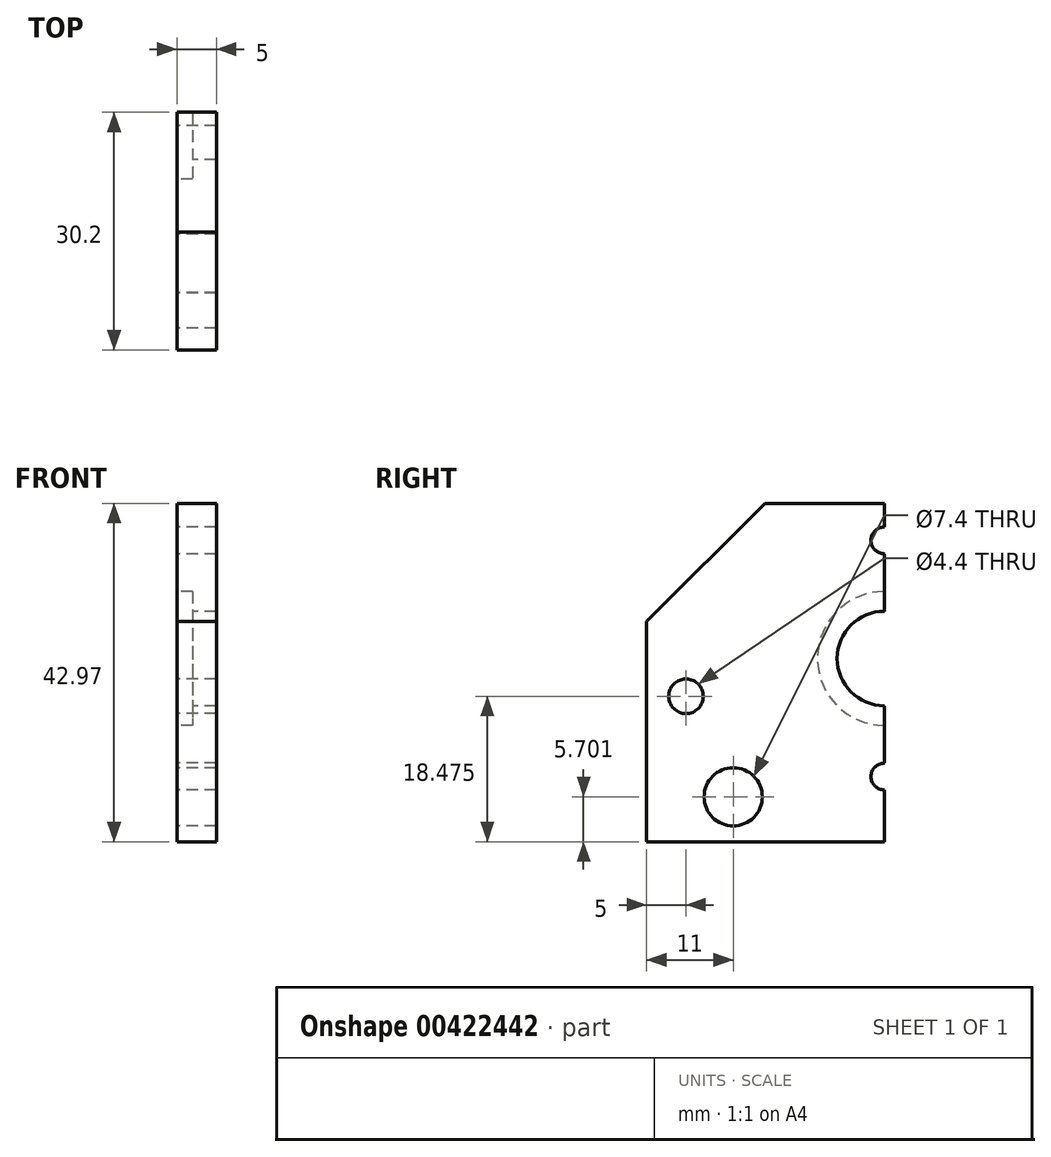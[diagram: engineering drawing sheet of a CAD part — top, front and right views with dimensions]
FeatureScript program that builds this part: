
annotation { "Feature Type Name" : "Feature", "Feature Type Description" : "" }
export const myFeature = defineFeature(function(context is Context, id is Id, definition is map)
    precondition{}
    {
        {
            var Q0;
            Q0=qCreatedBy(makeId("Right.planeOp"),FACE);
            var sketch = newSketch(context, id + "F0", { "sketchPlane" : qUnion([Q0])});
            skLineSegment(sketch, "E0.top", {"start": v(-63.57, 5.37) * mm, "end": v(-33.37, 5.37) * mm});
            skLineSegment(sketch, "E0.left", {"start": v(-63.57, 33.34) * mm, "end": v(-63.57, 5.37) * mm});
            skLineSegment(sketch, "E1", {"start": v(-48.57, 48.34) * mm, "end": v(-63.57, 33.34) * mm});
            skLineSegment(sketch, "E2", {"start": v(-48.57, 48.34) * mm, "end": v(-33.37, 48.34) * mm});
            skArc(sketch, "E3", {"start": v(-33.37, 37.14) * mm, "mid": v(-41.87, 28.64) * mm, "end": v(-33.37, 20.14) * mm});
            skPoint(sketch, "E3.first.point", {"position": v(-41.87, 28.44) * mm});
            skPoint(sketch, "E3.third.point", {"position": v(-33.88, 20.16) * mm});
            skArc(sketch, "E4", {"start": v(-33.37, 34.64) * mm, "mid": v(-39.37, 28.64) * mm, "end": v(-33.37, 22.64) * mm});
            skArc(sketch, "E5", {"start": v(-33.37, 45.34) * mm, "mid": v(-35.07, 43.64) * mm, "end": v(-33.37, 41.94) * mm});
            skPoint(sketch, "E5.first.point", {"position": v(-34.85, 44.47) * mm});
            skPoint(sketch, "E5.third.point", {"position": v(-34.4, 42.3) * mm});
            skCircle(sketch, "E6", {"center": v(-58.57, 23.84) * mm, "radius": 2.2 * mm});
            skPoint(sketch, "E6.first.point", {"position": v(-57.03, 25.41) * mm});
            skPoint(sketch, "E6.second.point", {"position": v(-60.74, 23.5) * mm});
            skPoint(sketch, "E6.third.point", {"position": v(-57.62, 21.86) * mm});
            skCircle(sketch, "E7", {"center": v(-52.57, 11.07) * mm, "radius": 3.7 * mm});
            skPoint(sketch, "E7.first.point", {"position": v(-50.08, 13.8) * mm});
            skPoint(sketch, "E7.second.point", {"position": v(-50.64, 7.91) * mm});
            skPoint(sketch, "E7.third.point", {"position": v(-56.25, 10.68) * mm});
            skArc(sketch, "E8", {"start": v(-33.37, 15.34) * mm, "mid": v(-35.07, 13.64) * mm, "end": v(-33.37, 11.94) * mm});
            skPoint(sketch, "E8.first.point", {"position": v(-33.72, 15.3) * mm});
            skPoint(sketch, "E8.second.point", {"position": v(-34.93, 12.96) * mm});
            skLineSegment(sketch, "E9", {"start": v(-33.37, 48.34) * mm, "end": v(-33.37, 5.37) * mm});
            skSolve(sketch);
        }
        {
            var Q0;
            Q0=makeQuery(id+"F0.imprint","IMPRINT",FACE,{"disambiguationData":[TD([[makeQuery(id+"F0.imprint","IMPRINT",EDGE,{"derivedFrom":sQuery(id+"F0.wireOp",EDGE,"E0.top")}),1.0]])]});
            extrude(context, id + "F1", {"entities" : qUnion([Q0]), "depth" : 5 * mm});
        }
        {
            var Q0;
            Q0=qSketchRegion(id+"F0",true);
            var Q1;
            Q1=makeQuery(id+"F0.imprint","IMPRINT",FACE,{"disambiguationData":[TD([[makeQuery(id+"F0.imprint","IMPRINT",EDGE,{"derivedFrom":sQuery(id+"F0.wireOp",EDGE,"E3")}),1.0]])]});
            extrude(context, id + "F2", {"entities" : qUnion([Q0, Q1]), "operationType" : NewBodyOperationType.ADD, "depth" : 3 * mm});
        }
        {
            var Q0;
            {var subQ0=sQuery(id+"F0.wireOp",EDGE,"E4");Q0=makeQuery(id+"F0.imprint","IMPRINT",FACE,{"disambiguationData":[TD([[makeQuery(id+"F0.imprint","IMPRINT",EDGE,{"derivedFrom":subQ0}),1.0]])]});}
            var Q1;
            {var subQ0=sQuery(id+"F0.wireOp",EDGE,"E5");Q1=makeQuery(id+"F0.imprint","IMPRINT",FACE,{"disambiguationData":[TD([[makeQuery(id+"F0.imprint","IMPRINT",EDGE,{"derivedFrom":subQ0}),1.0]])]});}
            var Q2;
            {var subQ0=sQuery(id+"F0.wireOp",EDGE,"E8");Q2=makeQuery(id+"F0.imprint","IMPRINT",FACE,{"disambiguationData":[TD([[makeQuery(id+"F0.imprint","IMPRINT",EDGE,{"derivedFrom":subQ0}),1.0]])]});}
            extrude(context, id + "F3", {"entities" : qUnion([Q0, Q1, Q2]), "operationType" : NewBodyOperationType.REMOVE, "endBound" : BoundingType.UP_TO_NEXT, "depth" : 25 * mm});
        }
        {
            var Q0;
            {var subQ0=sQuery(id+"F0.wireOp",EDGE,"E3");Q0=makeQuery(id+"F0.imprint","IMPRINT",FACE,{"disambiguationData":[TD([[makeQuery(id+"F0.imprint","IMPRINT",EDGE,{"derivedFrom":subQ0}),1.0]])]});}
            var Q1;
            {var subQ0=sQuery(id+"F0.wireOp",EDGE,"E9");var subQ1=sQuery(id+"F0.wireOp",EDGE,"E3");var subQ4=sQuery(id+"F0.wireOp",EDGE,"E2");var subQ5=sQuery(id+"F0.wireOp",EDGE,"E0.top");Q1=makeQuery(id+"F2.boolean.opBoolean","SPLIT",FACE,{"disambiguationData":[TD([makeQuery(id+"F1.opExtrude","SWEPT_FACE",FACE,{"disambiguationData":[OSD([subQ1])]})])],"derivedFrom":makeQuery(id+"F2.opExtrude","CAP_FACE",FACE,{"disambiguationData":[OSD([subQ5,sQuery(id+"F0.wireOp",EDGE,"E0.left"),sQuery(id+"F0.wireOp",EDGE,"E1"),subQ4,sQuery(id+"F0.wireOp",EDGE,"E6"),sQuery(id+"F0.wireOp",EDGE,"E7"),subQ0])],"isStart":false})});}
            var Q2;
            Q2=makeQuery(id+"F1.opExtrude","CAP_FACE",FACE,{"disambiguationData":[OSD([sQuery(id+"F0.wireOp",EDGE,"E0.top"),sQuery(id+"F0.wireOp",EDGE,"E0.left"),sQuery(id+"F0.wireOp",EDGE,"E1"),sQuery(id+"F0.wireOp",EDGE,"E2"),sQuery(id+"F0.wireOp",EDGE,"E3"),sQuery(id+"F0.wireOp",EDGE,"E5"),sQuery(id+"F0.wireOp",EDGE,"E6"),sQuery(id+"F0.wireOp",EDGE,"E7"),sQuery(id+"F0.wireOp",EDGE,"E8"),sQuery(id+"F0.wireOp",EDGE,"E9")])],"isStart":false});
            extrude(context, id + "F4", {"entities" : qUnion([Q0, Q1]), "operationType" : NewBodyOperationType.ADD, "endBound" : BoundingType.UP_TO_SURFACE, "endBoundEntityFace" : qUnion([Q2]), "depth" : 25 * mm});
        }
        {
            var Q0;
            {var subQ0=sQuery(id+"F0.wireOp",EDGE,"E3");Q0=makeQuery(id+"F0.imprint","IMPRINT",FACE,{"disambiguationData":[TD([[makeQuery(id+"F0.imprint","IMPRINT",EDGE,{"derivedFrom":subQ0}),1.0]])]});}
            extrude(context, id + "F5", {"entities" : qUnion([Q0]), "operationType" : NewBodyOperationType.REMOVE, "depth" : 2 * mm});
        }
    });
